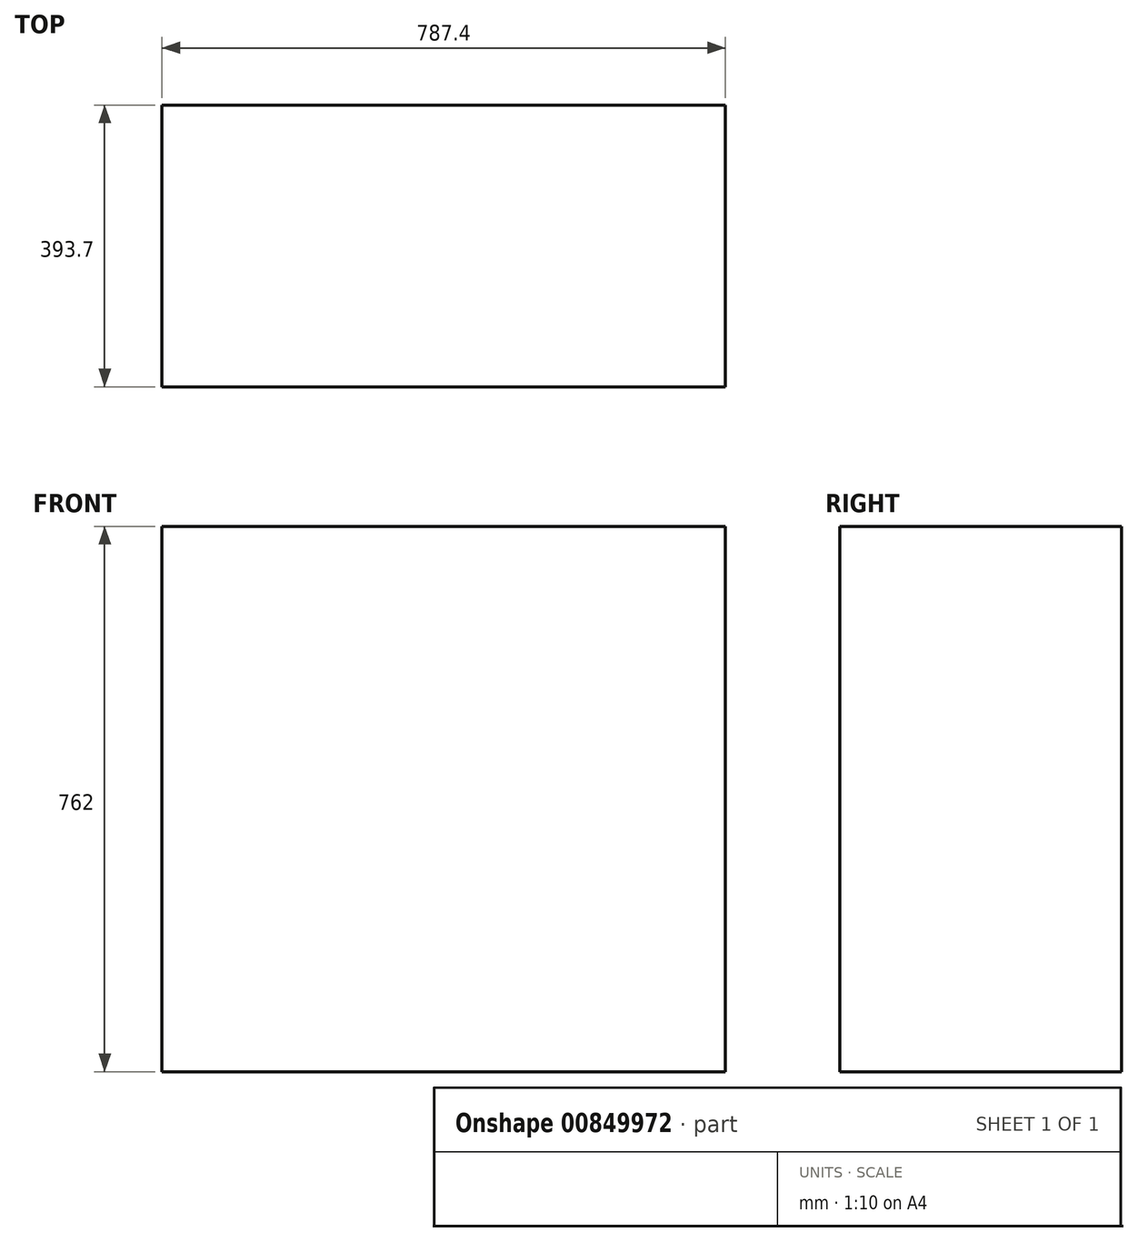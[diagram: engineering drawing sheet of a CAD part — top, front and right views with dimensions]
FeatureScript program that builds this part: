
annotation { "Feature Type Name" : "Feature", "Feature Type Description" : "" }
export const myFeature = defineFeature(function(context is Context, id is Id, definition is map)
    precondition{}
    {
        {
            var Q0;
            Q0=qCreatedBy(makeId("Top.planeOp"),FACE);
            var sketch = newSketch(context, id + "F0", { "sketchPlane" : qUnion([Q0])});
            skLineSegment(sketch, "E0.bottom", {"start": v(-393.7, 196.85) * mm, "end": v(393.7, 196.85) * mm});
            skLineSegment(sketch, "E0.top", {"start": v(-393.7, -196.85) * mm, "end": v(393.7, -196.85) * mm});
            skLineSegment(sketch, "E0.left", {"start": v(-393.7, 196.85) * mm, "end": v(-393.7, -196.85) * mm});
            skLineSegment(sketch, "E0.right", {"start": v(393.7, 196.85) * mm, "end": v(393.7, -196.85) * mm});
            skPoint(sketch, "E0.middle", {"position": v(0, 0) * mm});
            skSolve(sketch);
        }
        {
            var Q0;
            Q0 = qSketchRegion(id + "F0", true);
            extrude(context, id + "F1", {"entities" : qUnion([Q0]), "depth" : 762 * mm, "offsetDistance" : 25.4 * mm});
        }
    });
